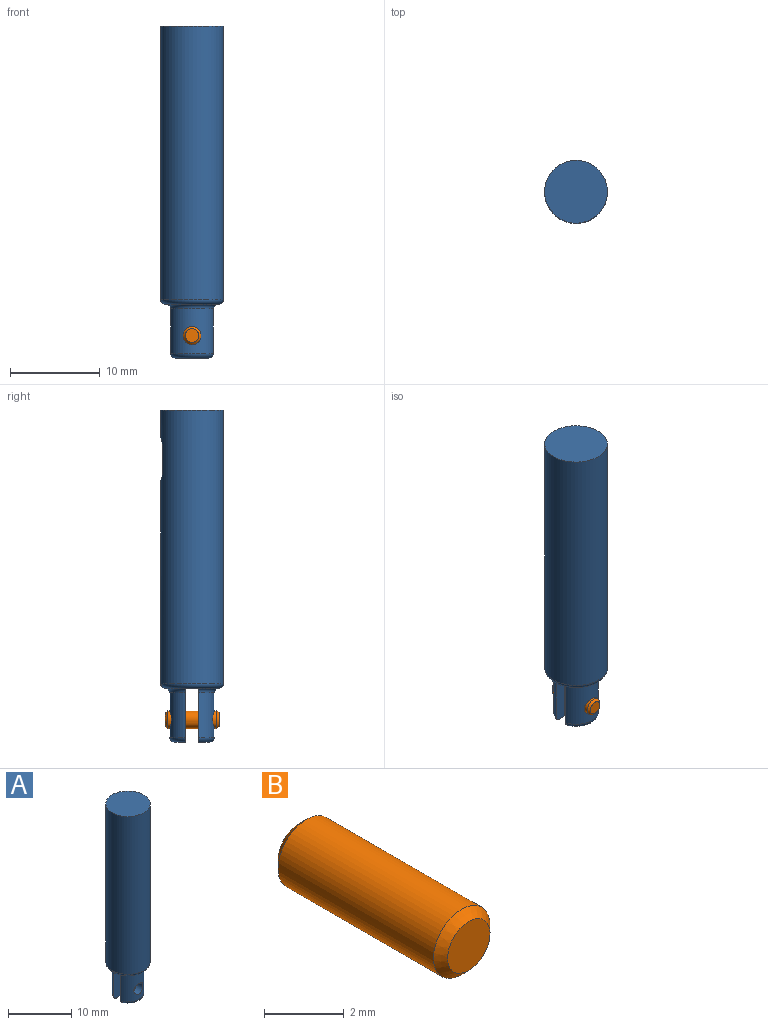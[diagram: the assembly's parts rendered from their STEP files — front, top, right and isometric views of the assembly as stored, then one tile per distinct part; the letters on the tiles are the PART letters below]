
ASSEMBLY  parts=2 mates=1
PART A: 28 faces, bbox 7.6x7.6x37 mm
  f0: plane 6x1.91mm, normal (0,1,0), area 8.3mm2, adj f2,f9,f10,f11,f13,f24,f26
  f1: plane 6x1.91mm, normal (0,-1,0), area 8.3mm2, adj f2,f4,f5,f6,f7,f24,f27
  f2: plane 2x1.5mm, normal (0,0,-1), area 2.7mm2, adj f0,f1,f12,f24
  f3: cylinder r=3.5mm len=30.5mm, axis (0,0,-1), area 659.3mm2, adj f8,f12,f19,f20,f21,f22
  f4: cylinder r=2.5mm len=5mm, axis (0,0,-1), area 28.4mm2, adj f1,f6,f7,f15,f17
  f5: plane 3.71x1.25mm, normal (0,0,-1), area 2.7mm2, adj f1,f7,f15,f27
  f6: torus R=3mm, axis (0,0,-1), area 5.4mm2, adj f1,f4,f12,f15
  f7: torus R=2mm, axis (0,0,1), area 4.5mm2, adj f1,f4,f5,f15
  f8: plane 7x7mm, normal (0,0,1), area 38.5mm2, adj f3
  f9: cylinder r=2.5mm len=5mm, axis (0,0,-1), area 28.4mm2, adj f0,f11,f13,f14,f18
  f10: plane 3.71x1.25mm, normal (0,0,-1), area 2.7mm2, adj f0,f13,f14,f26
  f11: torus R=3mm, axis (0,0,-1), area 5.4mm2, adj f0,f9,f12,f14
  f12: torus R=3mm, axis (0,0,-1), area 16.4mm2, adj f2,f3,f6,f11,f16
  f13: torus R=2mm, axis (0,0,1), area 4.5mm2, adj f0,f9,f10,f14
  f14: plane 6x1.91mm, normal (0,1,0), area 8.3mm2, adj f9,f10,f11,f13,f16,f24,f26
  f15: plane 6x1.91mm, normal (0,-1,0), area 8.3mm2, adj f4,f5,f6,f7,f16,f24,f27
  f16: plane 2x1.5mm, normal (0,0,-1), area 2.7mm2, adj f12,f14,f15,f24
  f17: cylinder r=1mm len=2mm, axis (0,-1,0), area 8.7mm2, adj f4,f24,f27
  f18: cylinder r=1mm len=2mm, axis (0,-1,0), area 8.7mm2, adj f9,f24,f26
  f19: cylinder r=1.25mm len=3.5mm, axis (0,-1,0), area 10.2mm2, adj f3,f20,f22,f24,f25
  f20: plane 3.27x2.5mm, normal (1,0,0), area 8.2mm2, adj f3,f19,f21,f24
  f21: cylinder r=1.25mm len=3.5mm, axis (0,-1,0), area 10.2mm2, adj f3,f20,f22,f24
  f22: plane 3.27x2.5mm, normal (-1,0,0), area 8.2mm2, adj f3,f19,f21,f24
  f23: plane 2.5x2.5mm, normal (0,0,-1), area 4.9mm2, adj f24,f25
  f24: cylinder r=1.25mm len=31.5mm, axis (0,0,1), area 215.7mm2, adj f0,f1,f2,f14,f15,f16,f17,f18
  f25: cylinder r=1.25mm len=1.25mm, axis (0,0,1), area 0.9mm2, adj f19,f23,f24
  f26: cylinder r=1.25mm len=2.5mm, axis (0,0,1), area 4.1mm2, adj f0,f10,f14,f18
  f27: cylinder r=1.25mm len=2.5mm, axis (0,0,1), area 4.1mm2, adj f1,f5,f15,f17
PART B: 5 faces, bbox 2x6x2 mm
  f0: cylinder r=1mm len=5.5mm, axis (0,1,0), area 34.6mm2, adj f3,f4
  f1: plane 1.5x1.5mm, normal (0,-1,0), area 1.8mm2, adj f3
  f2: plane 1.5x1.5mm, normal (0,1,0), area 1.8mm2, adj f4
  f3: cone r=0.75mm half-angle=45deg, axis (0,1,0), area 1.9mm2, adj f0,f1
  f4: cone r=1mm half-angle=45deg, axis (0,-1,0), area 1.9mm2, adj f0,f2
PLACE A at identity fixed
PLACE B t=(0,-0.01,0)mm
MATE fastened B.f0 <-> A.f17  axis (0,1,0) through (0,-0.01,-3.5)mm
